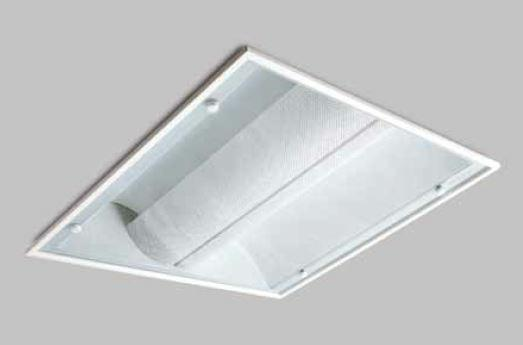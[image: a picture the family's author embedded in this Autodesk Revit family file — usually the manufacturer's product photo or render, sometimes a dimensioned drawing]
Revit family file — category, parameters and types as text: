
# Revit family: E 6060 GEC
name_source: partatom
category: Lighting Fixtures
revit_build: Autodesk Revit 2017 (Build: 20160225_1515(x64)
units: mm (PartAtom-declared; Revit-internal decimal feet)

## family parameters
Always vertical = Yes
Cut with Voids When Loaded = No
Host = Ceiling
Light Source = Yes
OmniClass Number = 23.80.70.11
OmniClass Title = Luminaries for Internal Lighting
Part Type = Normal
Room Calculation Point = No
Round Connector Dimension = Use Diameter
Shared = No

## types (2) — shared parameters
Apparent Load = 42 VA
Color Filter = 16777215
Dimming Lamp Color Temperature Shift = <None>
Emit Shape Visible in Rendering = Yes
Emit from Rectangle Length = 260 mm  [stored 0.853018 ft]
Emit from Rectangle Width = 560 mm  [stored 1.83727 ft]
Light Source Symbol Size = 610 mm
Manufacturer = ARLIGHT
Type Image = E 6060 GEC.JPG
Wattage Comments = 42

## type names (no varying parameters)
- EGEC.6060.42.30
- EGEC.6060.42.40

note: [stored X ft] marks values corroborated as IEEE doubles in the binary element streams (Revit-internal decimal feet)

## geometry (parser evidence)
native form markers: Sweep x3
no freeform markers — native parametric forms only
